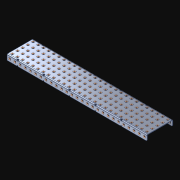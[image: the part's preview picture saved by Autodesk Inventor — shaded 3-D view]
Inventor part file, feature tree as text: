
AUTODESK INVENTOR PART (.ipt)
format: ipt  version: 2021 (Build 250183000, 183)  size: 2,230,784 bytes
history: native  units: in
note: dims shown in document units (in); Inventor stores cm internally (conversion verified against a paired STEP export)
features: extrude x190, other x190, sketch x4, pattern_linear x3
ambient origin geometry x8: Origin, YZ Plane, XZ Plane, XY Plane, X Axis, Y Axis, Z Axis, Center Point
bodies: Solid1 (feature_tree)
feature tree (387):
  pattern_linear  "Rectangular Pattern1"  Spacing1=0.182in  [1 undecoded]
  pattern_linear  "Rectangular Pattern2"  Spacing1=0.046in  [1 undecoded]
  pattern_linear  "Rectangular Pattern3"  Spacing1=0.5in  [1 undecoded]
  extrude  "Extrusion1"  Depth=0.046in
  sketch  "Sketch1"  dims[d0=0.182in]
  other  "Srf1"
  sketch  "Sketch2"  dims[d1=0.046in d2=0.0in]
  other  "Srf2"
  sketch  "Sketch3"  dims[d3=0.182in]
  other  "Srf3"
  other  "Srf4"
  other  "Srf5"
  other  "Srf6"
  other  "Srf7"
  other  "Srf8"
  other  "Srf9"
  other  "Srf10"
  other  "Srf11"
  other  "Srf12"
  other  "Srf13"
  other  "Srf14"
  other  "Srf15"
  other  "Srf16"
  other  "Srf17"
  other  "Srf18"
  other  "Srf19"
  other  "Srf20"
  other  "Srf21"
  other  "Srf22"
  other  "Srf23"
  other  "Srf24"
  other  "Srf25"
  other  "Srf26"
  other  "Srf27"
  other  "Srf28"
  other  "Srf29"
  other  "Srf38"
  other  "Srf39"
  other  "Srf40"
  other  "Srf41"
  other  "Srf42"
  other  "Srf43"
  other  "Srf44"
  other  "Srf45"
  other  "Srf46"
  other  "Srf47"
  other  "Srf48"
  other  "Srf49"
  other  "Srf50"
  other  "Srf51"
  other  "Srf52"
  other  "Srf53"
  other  "Srf54"
  other  "Srf55"
  other  "Srf56"
  other  "Srf57"
  other  "Srf58"
  other  "Srf59"
  other  "Srf60"
  other  "Srf61"
  other  "Srf62"
  other  "Srf63"
  other  "Srf72"
  other  "Srf73"
  other  "Srf74"
  other  "Srf75"
  other  "Srf76"
  other  "Srf77"
  other  "Srf78"
  other  "Srf79"
  other  "Srf80"
  other  "Srf81"
  other  "Srf82"
  other  "Srf83"
  other  "Srf84"
  other  "Srf85"
  other  "Srf86"
  other  "Srf87"
  other  "Srf88"
  other  "Srf89"
  other  "Srf90"
  other  "Srf91"
  other  "Srf92"
  other  "Srf93"
  other  "Srf94"
  other  "Srf95"
  other  "Srf96"
  other  "Srf97"
  other  "Srf98"
  other  "Srf107"
  other  "Srf108"
  other  "Srf109"
  other  "Srf110"
  other  "Srf111"
  other  "Srf112"
  other  "Srf113"
  other  "Srf114"
  other  "Srf115"
  other  "Srf116"
  other  "Srf117"
  other  "Srf118"
  other  "Srf119"
  other  "Srf120"
  other  "Srf121"
  other  "Srf122"
  other  "Srf123"
  other  "Srf124"
  other  "Srf125"
  other  "Srf126"
  other  "Srf127"
  other  "Srf128"
  other  "Srf129"
  other  "Srf130"
  other  "Srf131"
  other  "Srf132"
  other  "Srf133"
  other  "Srf142"
  other  "Srf143"
  other  "Srf144"
  other  "Srf145"
  other  "Srf146"
  other  "Srf147"
  other  "Srf148"
  other  "Srf149"
  other  "Srf150"
  other  "Srf151"
  other  "Srf152"
  other  "Srf153"
  other  "Srf154"
  other  "Srf155"
  other  "Srf156"
  other  "Srf157"
  other  "Srf158"
  other  "Srf159"
  other  "Srf160"
  other  "Srf161"
  other  "Srf162"
  other  "Srf163"
  other  "Srf164"
  other  "Srf165"
  other  "Srf166"
  other  "Srf167"
  other  "Srf168"
  other  "Srf177"
  other  "Srf178"
  other  "Srf179"
  other  "Srf180"
  other  "Srf181"
  other  "Srf182"
  other  "Srf183"
  other  "Srf184"
  other  "Srf185"
  other  "Srf186"
  other  "Srf187"
  other  "Srf188"
  other  "Srf189"
  other  "Srf190"
  other  "Srf191"
  other  "Srf192"
  other  "Srf193"
  other  "Srf194"
  other  "Srf195"
  other  "Srf196"
  other  "Srf197"
  other  "Srf198"
  other  "Srf199"
  other  "Srf200"
  other  "Srf201"
  other  "Srf202"
  other  "Srf203"
  other  "Srf212"
  other  "Srf213"
  other  "Srf214"
  other  "Srf215"
  other  "Srf216"
  other  "Srf217"
  other  "Srf218"
  other  "Srf219"
  other  "Srf220"
  other  "Srf221"
  other  "Srf222"
  other  "Srf223"
  other  "Srf224"
  other  "Srf225"
  other  "Srf226"
  other  "Srf227"
  other  "Srf228"
  other  "Srf229"
  other  "Srf230"
  other  "Srf231"
  other  "Srf232"
  other  "Srf233"
  other  "Srf234"
  other  "Srf235"
  other  "Srf236"
  other  "Srf237"
  sketch  "Sketch4"  dims[d4=0.046in d5=0.0in d6=0.182in d7=0.046in d8=0.0in d11=0.5in d12=10.6299in d14=0.5in d15=1.9685in d17=0.5in d18=10.6299in d20=0.5in d21=4.0in d22=0.0in]
  parser-record x1  (decoder bookkeeping rows leaked as tree rows — omitted from the tree; the rows remain in map.json)
  extrude  "ExtrusionSrf1"  Depth=0.046in
  extrude  "ExtrusionSrf2"  Depth=0.046in
  extrude  "ExtrusionSrf3"  Depth=0.046in
  extrude  "ExtrusionSrf4"  Depth=0.046in
  extrude  "ExtrusionSrf5"  Depth=0.046in
  extrude  "ExtrusionSrf6"  TaperAngle=0.0deg  [1 undecoded]
  extrude  "ExtrusionSrf7"  [1 undecoded]
  extrude  "ExtrusionSrf8"  [1 undecoded]
  extrude  "ExtrusionSrf9"  [1 undecoded]
  extrude  "ExtrusionSrf10"  [1 undecoded]
  extrude  "ExtrusionSrf11"  [1 undecoded]
  extrude  "ExtrusionSrf12"  [1 undecoded]
  extrude  "ExtrusionSrf13"  [1 undecoded]
  extrude  "ExtrusionSrf14"  [1 undecoded]
  extrude  "ExtrusionSrf15"  [1 undecoded]
  extrude  "ExtrusionSrf16"  [1 undecoded]
  extrude  "ExtrusionSrf17"  [1 undecoded]
  extrude  "ExtrusionSrf18"  [1 undecoded]
  extrude  "ExtrusionSrf19"  [1 undecoded]
  extrude  "ExtrusionSrf20"  [1 undecoded]
  extrude  "ExtrusionSrf21"  [1 undecoded]
  extrude  "ExtrusionSrf22"  [1 undecoded]
  extrude  "ExtrusionSrf23"  [1 undecoded]
  extrude  "ExtrusionSrf24"  [1 undecoded]
  extrude  "ExtrusionSrf25"  [1 undecoded]
  extrude  "ExtrusionSrf26"  [1 undecoded]
  extrude  "ExtrusionSrf27"  [1 undecoded]
  extrude  "ExtrusionSrf28"  [1 undecoded]
  extrude  "ExtrusionSrf29"  [1 undecoded]
  extrude  "ExtrusionSrf38"  [1 undecoded]
  extrude  "ExtrusionSrf39"  [1 undecoded]
  extrude  "ExtrusionSrf40"  [1 undecoded]
  extrude  "ExtrusionSrf41"  [1 undecoded]
  extrude  "ExtrusionSrf42"  [1 undecoded]
  extrude  "ExtrusionSrf43"  [1 undecoded]
  extrude  "ExtrusionSrf44"  [1 undecoded]
  extrude  "ExtrusionSrf45"  [1 undecoded]
  extrude  "ExtrusionSrf46"  [1 undecoded]
  extrude  "ExtrusionSrf47"  [1 undecoded]
  extrude  "ExtrusionSrf48"  [1 undecoded]
  extrude  "ExtrusionSrf49"  [1 undecoded]
  extrude  "ExtrusionSrf50"  [1 undecoded]
  extrude  "ExtrusionSrf51"  [1 undecoded]
  extrude  "ExtrusionSrf52"  [1 undecoded]
  extrude  "ExtrusionSrf53"  [1 undecoded]
  extrude  "ExtrusionSrf54"  [1 undecoded]
  extrude  "ExtrusionSrf55"  [1 undecoded]
  extrude  "ExtrusionSrf56"  [1 undecoded]
  extrude  "ExtrusionSrf57"  [1 undecoded]
  extrude  "ExtrusionSrf58"  [1 undecoded]
  extrude  "ExtrusionSrf59"  [1 undecoded]
  extrude  "ExtrusionSrf60"  [1 undecoded]
  extrude  "ExtrusionSrf61"  [1 undecoded]
  extrude  "ExtrusionSrf62"  [1 undecoded]
  extrude  "ExtrusionSrf63"  [1 undecoded]
  extrude  "ExtrusionSrf72"  [1 undecoded]
  extrude  "ExtrusionSrf73"  [1 undecoded]
  extrude  "ExtrusionSrf74"  [1 undecoded]
  extrude  "ExtrusionSrf75"  [1 undecoded]
  extrude  "ExtrusionSrf76"  [1 undecoded]
  extrude  "ExtrusionSrf77"  [1 undecoded]
  extrude  "ExtrusionSrf78"  [1 undecoded]
  extrude  "ExtrusionSrf79"  [1 undecoded]
  extrude  "ExtrusionSrf80"  [1 undecoded]
  extrude  "ExtrusionSrf81"  [1 undecoded]
  extrude  "ExtrusionSrf82"  [1 undecoded]
  extrude  "ExtrusionSrf83"  [1 undecoded]
  extrude  "ExtrusionSrf84"  [1 undecoded]
  extrude  "ExtrusionSrf85"  [1 undecoded]
  extrude  "ExtrusionSrf86"  [1 undecoded]
  extrude  "ExtrusionSrf87"  [1 undecoded]
  extrude  "ExtrusionSrf88"  [1 undecoded]
  extrude  "ExtrusionSrf89"  [1 undecoded]
  extrude  "ExtrusionSrf90"  [1 undecoded]
  extrude  "ExtrusionSrf91"  [1 undecoded]
  extrude  "ExtrusionSrf92"  [1 undecoded]
  extrude  "ExtrusionSrf93"  [1 undecoded]
  extrude  "ExtrusionSrf94"  [1 undecoded]
  extrude  "ExtrusionSrf95"  [1 undecoded]
  extrude  "ExtrusionSrf96"  [1 undecoded]
  extrude  "ExtrusionSrf97"  [1 undecoded]
  extrude  "ExtrusionSrf98"  [1 undecoded]
  extrude  "ExtrusionSrf107"  [1 undecoded]
  extrude  "ExtrusionSrf108"  [1 undecoded]
  extrude  "ExtrusionSrf109"  [1 undecoded]
  extrude  "ExtrusionSrf110"  [1 undecoded]
  extrude  "ExtrusionSrf111"  [1 undecoded]
  extrude  "ExtrusionSrf112"  [1 undecoded]
  extrude  "ExtrusionSrf113"  [1 undecoded]
  extrude  "ExtrusionSrf114"  [1 undecoded]
  extrude  "ExtrusionSrf115"  [1 undecoded]
  extrude  "ExtrusionSrf116"  [1 undecoded]
  extrude  "ExtrusionSrf117"  [1 undecoded]
  extrude  "ExtrusionSrf118"  [1 undecoded]
  extrude  "ExtrusionSrf119"  [1 undecoded]
  extrude  "ExtrusionSrf120"  [1 undecoded]
  extrude  "ExtrusionSrf121"  [1 undecoded]
  extrude  "ExtrusionSrf122"  [1 undecoded]
  extrude  "ExtrusionSrf123"  [1 undecoded]
  extrude  "ExtrusionSrf124"  [1 undecoded]
  extrude  "ExtrusionSrf125"  [1 undecoded]
  extrude  "ExtrusionSrf126"  [1 undecoded]
  extrude  "ExtrusionSrf127"  [1 undecoded]
  extrude  "ExtrusionSrf128"  [1 undecoded]
  extrude  "ExtrusionSrf129"  [1 undecoded]
  extrude  "ExtrusionSrf130"  [1 undecoded]
  extrude  "ExtrusionSrf131"  [1 undecoded]
  extrude  "ExtrusionSrf132"  [1 undecoded]
  extrude  "ExtrusionSrf133"  [1 undecoded]
  extrude  "ExtrusionSrf142"  [1 undecoded]
  extrude  "ExtrusionSrf143"  [1 undecoded]
  extrude  "ExtrusionSrf144"  [1 undecoded]
  extrude  "ExtrusionSrf145"  [1 undecoded]
  extrude  "ExtrusionSrf146"  [1 undecoded]
  extrude  "ExtrusionSrf147"  [1 undecoded]
  extrude  "ExtrusionSrf148"  [1 undecoded]
  extrude  "ExtrusionSrf149"  [1 undecoded]
  extrude  "ExtrusionSrf150"  [1 undecoded]
  extrude  "ExtrusionSrf151"  [1 undecoded]
  extrude  "ExtrusionSrf152"  [1 undecoded]
  extrude  "ExtrusionSrf153"  [1 undecoded]
  extrude  "ExtrusionSrf154"  [1 undecoded]
  extrude  "ExtrusionSrf155"  [1 undecoded]
  extrude  "ExtrusionSrf156"  [1 undecoded]
  extrude  "ExtrusionSrf157"  [1 undecoded]
  extrude  "ExtrusionSrf158"  [1 undecoded]
  extrude  "ExtrusionSrf159"  [1 undecoded]
  extrude  "ExtrusionSrf160"  [1 undecoded]
  extrude  "ExtrusionSrf161"  [1 undecoded]
  extrude  "ExtrusionSrf162"  [1 undecoded]
  extrude  "ExtrusionSrf163"  [1 undecoded]
  extrude  "ExtrusionSrf164"  [1 undecoded]
  extrude  "ExtrusionSrf165"  [1 undecoded]
  extrude  "ExtrusionSrf166"  [1 undecoded]
  extrude  "ExtrusionSrf167"  [1 undecoded]
  extrude  "ExtrusionSrf168"  [1 undecoded]
  extrude  "ExtrusionSrf177"  [1 undecoded]
  extrude  "ExtrusionSrf178"  [1 undecoded]
  extrude  "ExtrusionSrf179"  [1 undecoded]
  extrude  "ExtrusionSrf180"  [1 undecoded]
  extrude  "ExtrusionSrf181"  [1 undecoded]
  extrude  "ExtrusionSrf182"  [1 undecoded]
  extrude  "ExtrusionSrf183"  [1 undecoded]
  extrude  "ExtrusionSrf184"  [1 undecoded]
  extrude  "ExtrusionSrf185"  [1 undecoded]
  extrude  "ExtrusionSrf186"  [1 undecoded]
  extrude  "ExtrusionSrf187"  [1 undecoded]
  extrude  "ExtrusionSrf188"  [1 undecoded]
  extrude  "ExtrusionSrf189"  [1 undecoded]
  extrude  "ExtrusionSrf190"  [1 undecoded]
  extrude  "ExtrusionSrf191"  [1 undecoded]
  extrude  "ExtrusionSrf192"  [1 undecoded]
  extrude  "ExtrusionSrf193"  [1 undecoded]
  extrude  "ExtrusionSrf194"  [1 undecoded]
  extrude  "ExtrusionSrf195"  [1 undecoded]
  extrude  "ExtrusionSrf196"  [1 undecoded]
  extrude  "ExtrusionSrf197"  [1 undecoded]
  extrude  "ExtrusionSrf198"  [1 undecoded]
  extrude  "ExtrusionSrf199"  [1 undecoded]
  extrude  "ExtrusionSrf200"  [1 undecoded]
  extrude  "ExtrusionSrf201"  [1 undecoded]
  extrude  "ExtrusionSrf202"  [1 undecoded]
  extrude  "ExtrusionSrf203"  [1 undecoded]
  extrude  "ExtrusionSrf212"  [1 undecoded]
  extrude  "ExtrusionSrf213"  [1 undecoded]
  extrude  "ExtrusionSrf214"  [1 undecoded]
  extrude  "ExtrusionSrf215"  [1 undecoded]
  extrude  "ExtrusionSrf216"  [1 undecoded]
  extrude  "ExtrusionSrf217"  [1 undecoded]
  extrude  "ExtrusionSrf218"  [1 undecoded]
  extrude  "ExtrusionSrf219"  [1 undecoded]
  extrude  "ExtrusionSrf220"  [1 undecoded]
  extrude  "ExtrusionSrf221"  [1 undecoded]
  extrude  "ExtrusionSrf222"  [1 undecoded]
  extrude  "ExtrusionSrf223"  [1 undecoded]
  extrude  "ExtrusionSrf224"  [1 undecoded]
  extrude  "ExtrusionSrf225"  [1 undecoded]
  extrude  "ExtrusionSrf226"  [1 undecoded]
  extrude  "ExtrusionSrf227"  [1 undecoded]
  extrude  "ExtrusionSrf228"  [1 undecoded]
  extrude  "ExtrusionSrf229"  [1 undecoded]
  extrude  "ExtrusionSrf230"  [1 undecoded]
  extrude  "ExtrusionSrf231"  [1 undecoded]
  extrude  "ExtrusionSrf232"  [1 undecoded]
  extrude  "ExtrusionSrf233"  [1 undecoded]
  extrude  "ExtrusionSrf234"  [1 undecoded]
  extrude  "ExtrusionSrf235"  [1 undecoded]
  extrude  "ExtrusionSrf236"  [1 undecoded]
  extrude  "ExtrusionSrf237"  [1 undecoded]
note: 187 required parameter values undecoded (feature->parameter linkage not recoverable at this tier; creation-order binding heuristic only, values carry confidence <= 0.55)
